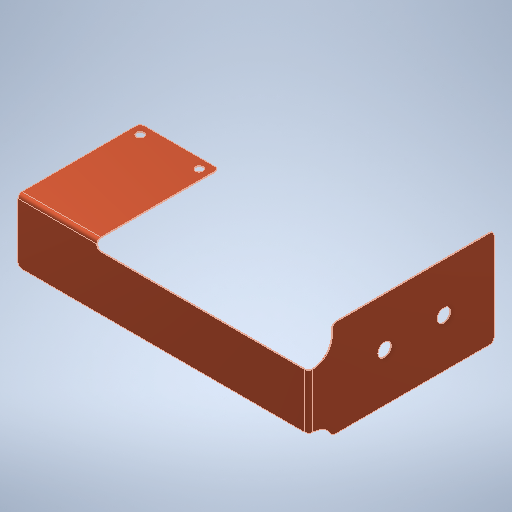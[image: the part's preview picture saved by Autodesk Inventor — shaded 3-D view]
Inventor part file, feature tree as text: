
AUTODESK INVENTOR PART (.ipt)
format: ipt  version: 2025 (Build 290162000, 162)  size: 352,768 bytes
history: native  units: mm
features: sketch x8, extrude x6, hole x2, fillet x1
ambient origin geometry x8: Origin, YZ Plane, XZ Plane, XY Plane, X Axis, Y Axis, Z Axis, Center Point
bodies: Solid1 (feature_tree)
feature tree (17):
  extrude  "Extrusion1"  Depth=10.0mm
  extrude  "Extrusion2"  Depth=0.2mm TaperAngle=0.0deg
  extrude  "Extrusion3"  Depth=1.0mm
  extrude  "Extrusion4"  Depth=0.2mm
  extrude  "Extrusion5"  Depth=0.2mm TaperAngle=0.0deg
  extrude  "Extrusion6"  TaperAngle=90.0deg  [1 undecoded]
  fillet  "Fillet1"  Radius=1.0mm
  hole  "Hole1"  [1 undecoded]
  hole  "Hole2"  [1 undecoded]
  sketch  "Sketch1"  dims[d0=20.0mm d1=10.0mm]
  sketch  "Sketch2"  dims[d2=30.0mm d3=0.2mm d4=0.0mm]
  sketch  "Sketch3"  dims[d5=90.0deg d6=1.0mm]
  sketch  "Sketch4"  dims[d7=0.2mm d8=0.2mm]
  sketch  "Sketch5"  dims[d9=15.0mm d10=0.2mm d11=0.0mm]
  sketch  "Sketch6"  dims[d12=52.7mm d13=0.0mm d14=90.0deg d15=1.0mm]
  sketch  "Sketch7"  dims[d16=46.0mm d17=50.0mm d18=0.0mm]
  sketch  "Sketch8"  dims[d19=1.2mm d20=7.5mm d21=5.0mm d22=5.0mm d23=10.0mm d24=0.0mm d25=10.0mm d26=0.0mm d27=1.0mm d28=0.2mm d29=2.5mm d30=2.5mm d31=2.5mm d32=2.0mm d33=6.0mm d34=9.4mm d35=2.0mm d36=90.0deg d37=7.9mm d38=20.594885mm d39=24.511926mm d40=12.255963mm d41=15.0mm d42=12.74mm d43=3.4mm d44=6.0mm d45=6.3mm d46=2.0mm d47=90.0deg d48=7.9mm d49=20.594885mm]
note: 3 required parameter values undecoded (feature->parameter linkage not recoverable at this tier; creation-order binding heuristic only, values carry confidence <= 0.55)
